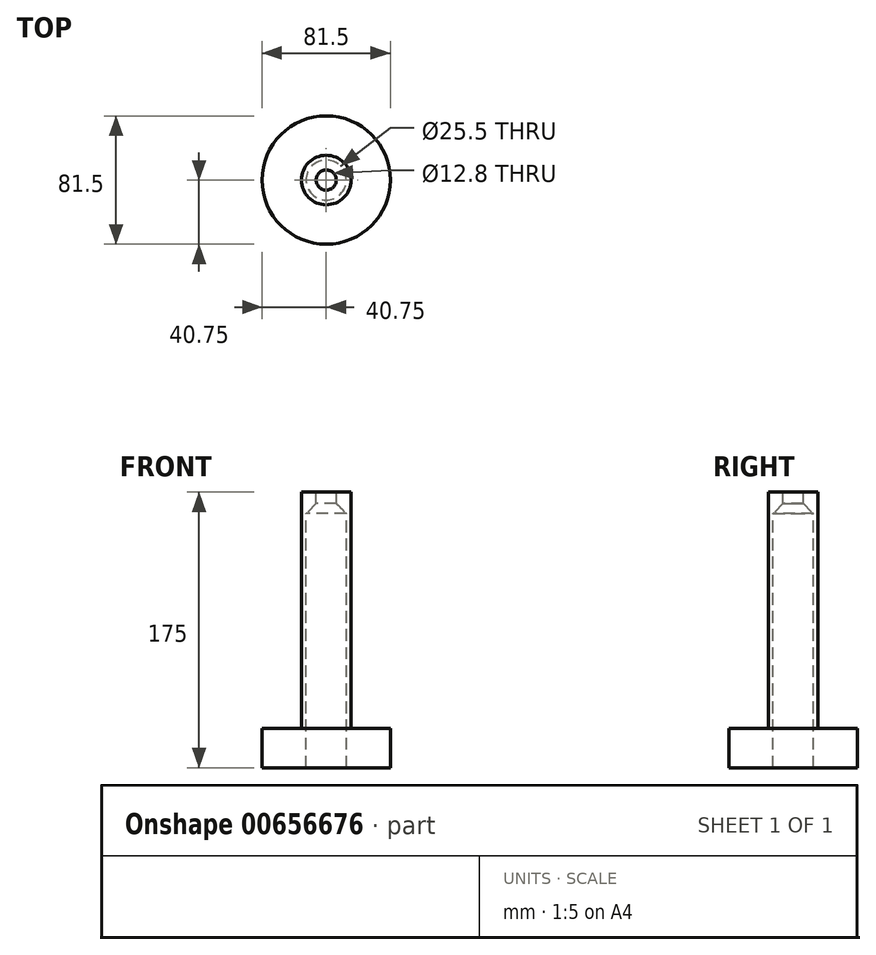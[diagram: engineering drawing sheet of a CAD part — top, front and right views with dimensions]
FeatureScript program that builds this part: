
annotation { "Feature Type Name" : "Feature", "Feature Type Description" : "" }
export const myFeature = defineFeature(function(context is Context, id is Id, definition is map)
    precondition{}
    {
        {
            var Q0;
            Q0=qCreatedBy(makeId("Front.planeOp"),FACE);
            var sketch = newSketch(context, id + "F0", { "sketchPlane" : qUnion([Q0])});
            skLineSegment(sketch, "E0", {"start": v(0, 0) * mm, "end": v(0, 150) * mm, "construction": true});
            skLineSegment(sketch, "E1.bottom", {"start": v(15.75, 0) * mm, "end": v(12.75, 0) * mm});
            skLineSegment(sketch, "E1.top", {"start": v(15.75, 150) * mm, "end": v(12.75, 150) * mm});
            skLineSegment(sketch, "E1.left", {"start": v(15.75, 0) * mm, "end": v(15.75, 150) * mm});
            skLineSegment(sketch, "E1.right", {"start": v(12.75, 0) * mm, "end": v(12.75, 150) * mm});
            skLineSegment(sketch, "E2.bottom", {"start": v(12.75, 150) * mm, "end": v(40.75, 150) * mm});
            skLineSegment(sketch, "E2.top", {"start": v(12.75, 175) * mm, "end": v(40.75, 175) * mm});
            skLineSegment(sketch, "E2.left", {"start": v(12.75, 150) * mm, "end": v(12.75, 175) * mm});
            skLineSegment(sketch, "E2.right", {"start": v(40.75, 150) * mm, "end": v(40.75, 175) * mm});
            skLineSegment(sketch, "E3", {"start": v(12.75, 13.55) * mm, "end": v(6.4, 7.2) * mm});
            skLineSegment(sketch, "E4", {"start": v(6.4, 7.2) * mm, "end": v(6.4, 0) * mm});
            skLineSegment(sketch, "E5", {"start": v(6.4, 0) * mm, "end": v(12.75, 0) * mm});
            skLineSegment(sketch, "E6", {"start": v(12.75, 13.55) * mm, "end": v(15.75, 16.55) * mm, "construction": true});
            skSolve(sketch);
        }
        {
            var Q0;
            {var subQ2=sQuery(id+"F0.wireOp",EDGE,"E1.top");var subQ3=sQuery(id+"F0.wireOp",EDGE,"E3");var subQ5=makeQuery(id+"F0.imprint","IMPRINT",EDGE,{"derivedFrom":subQ2});var subQ6=sQuery(id+"F0.wireOp",EDGE,"E1.bottom");Q0=qUnion([makeQuery(id+"F0.imprint","IMPRINT",FACE,{"disambiguationData":[TD([[subQ5,-1.0]])]}),makeQuery(id+"F0.imprint","IMPRINT",FACE,{"disambiguationData":[TD([[makeQuery(id+"F0.imprint","IMPRINT",EDGE,{"derivedFrom":subQ3}),1.0]])]}),makeQuery(id+"F0.imprint","IMPRINT",FACE,{"disambiguationData":[TD([[makeQuery(id+"F0.imprint","IMPRINT",EDGE,{"derivedFrom":subQ6}),-1.0]])]})]);}
            var Q1;
            Q1=sQuery(id+"F0.wireOp",EDGE,"E0");
            revolve(context, id + "F1", {"entities" : qUnion([Q0]), "axis" : qUnion([Q1]), "revolveType" : RevolveType.FULL});
        }
        {
            var Q0;
            Q0=qCreatedBy(makeId("Top.planeOp"),FACE);
            var sketch = newSketch(context, id + "F2", { "sketchPlane" : qUnion([Q0])});
            skLineSegment(sketch, "E7", {"start": v(0, 0) * mm, "end": v(0, 50.52) * mm});
            skSolve(sketch);
        }
        {
            var Q0;
            Q0=makeQuery(id+"F1.opRevolve","SWEPT_BODY",BODY,{"disambiguationData":[OSD([sQuery(id+"F0.wireOp",EDGE,"E1.bottom"),sQuery(id+"F0.wireOp",EDGE,"E1.left"),sQuery(id+"F0.wireOp",EDGE,"E1.right"),sQuery(id+"F0.wireOp",EDGE,"E2.bottom"),sQuery(id+"F0.wireOp",EDGE,"E2.top"),sQuery(id+"F0.wireOp",EDGE,"E2.left"),sQuery(id+"F0.wireOp",EDGE,"E2.right"),sQuery(id+"F0.wireOp",EDGE,"E3"),sQuery(id+"F0.wireOp",EDGE,"E4"),sQuery(id+"F0.wireOp",EDGE,"E5")])]});
            var Q1;
            Q1=sQuery(id+"F2.wireOp",EDGE,"E7");
            var Q2;
            Q2=sQuery(id+"F2.wireOp",EDGE,"E7");
            transform(context, id + "F3", {"entities" : qUnion([Q0]), "transformType" : TransformType.ROTATION, "transformAxis" : qUnion([Q2]), "angle" : 180 * degree, "makeCopy" : false});
        }
    });
